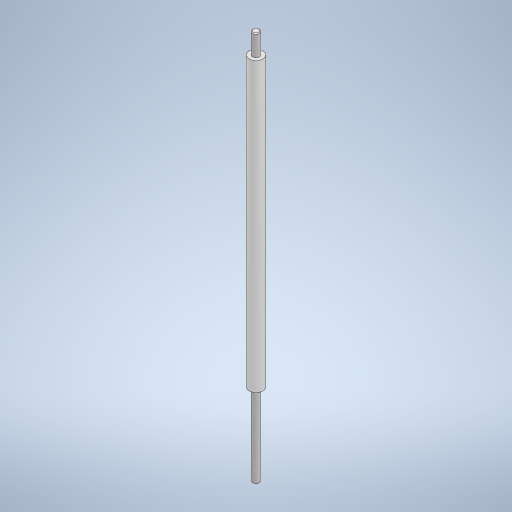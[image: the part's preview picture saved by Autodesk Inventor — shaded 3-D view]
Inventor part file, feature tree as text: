
AUTODESK INVENTOR PART (.ipt)
format: ipt  version: 2024.3 (Build 283343000, 343)  size: 253,952 bytes
history: native  units: mm
features: other x1, revolve x1, thread x1, chamfer x1, sketch x1
ambient origin geometry x8: Origin, YZ Plane, XZ Plane, XY Plane, X Axis, Y Axis, Z Axis, Center Point
bodies: Body1 (feature_tree)
feature tree (5):
  other  "Sólido1"
  revolve  "Revolución1"  [1 undecoded]
  thread  "Rosca1"  [1 undecoded]
  chamfer  "Chaflán1"  Distance=123.0mm
  sketch  "Boceto1"  dims[d1=3.0mm d2=6.0mm d3=9.0mm d4=123.0mm d5=90.0deg d6=144.0mm d7=0.0mm d8=35.0mm d9=0.306725mm d10=2.0mm d11=45.0deg]
note: 2 required parameter values undecoded (feature->parameter linkage not recoverable at this tier; creation-order binding heuristic only, values carry confidence <= 0.55)